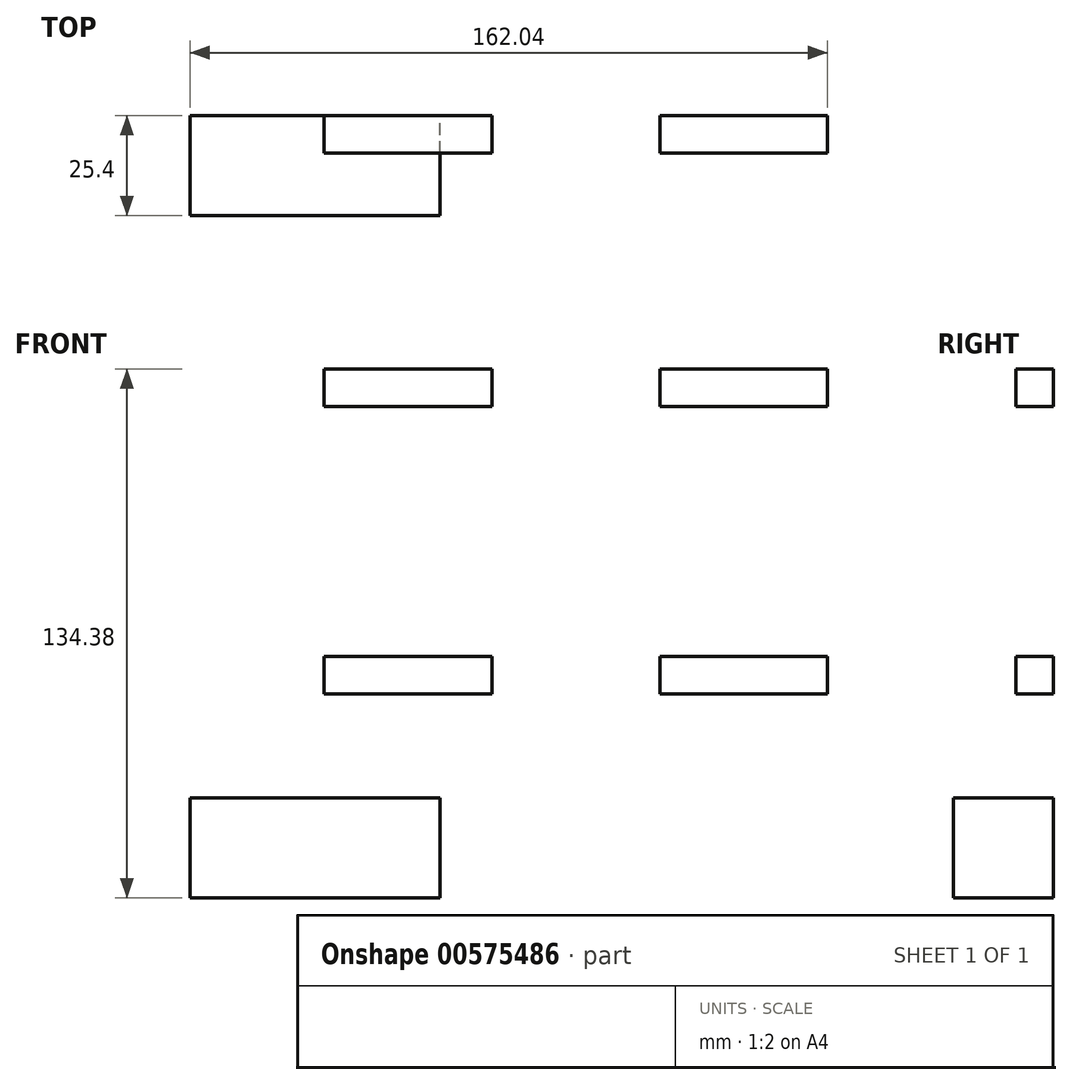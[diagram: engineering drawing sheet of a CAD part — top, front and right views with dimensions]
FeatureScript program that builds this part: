
annotation { "Feature Type Name" : "Feature", "Feature Type Description" : "" }
export const myFeature = defineFeature(function(context is Context, id is Id, definition is map)
    precondition{}
    {
        {
            var Q0;
            Q0=qCreatedBy(makeId("Front.planeOp"),FACE);
            var sketch = newSketch(context, id + "F0", { "sketchPlane" : qUnion([Q0])});
            skLineSegment(sketch, "E0.bottom", {"start": v(-119, 86.33) * mm, "end": v(51.66, 86.33) * mm});
            skLineSegment(sketch, "E0.top", {"start": v(-119, 3.78) * mm, "end": v(51.66, 3.78) * mm});
            skLineSegment(sketch, "E0.left", {"start": v(-119, 86.33) * mm, "end": v(-119, 3.78) * mm});
            skLineSegment(sketch, "E0.right", {"start": v(51.66, 86.33) * mm, "end": v(51.66, 3.78) * mm});
            skLineSegment(sketch, "E1.bottom", {"start": v(-119, 3.78) * mm, "end": v(-76.34, 3.78) * mm});
            skLineSegment(sketch, "E1.top", {"start": v(-119, 13.3) * mm, "end": v(-76.34, 13.3) * mm});
            skLineSegment(sketch, "E1.left", {"start": v(-119, 3.78) * mm, "end": v(-119, 13.3) * mm});
            skLineSegment(sketch, "E1.right", {"start": v(-76.34, 3.78) * mm, "end": v(-76.34, 13.3) * mm});
            skLineSegment(sketch, "E2.bottom", {"start": v(-76.34, 13.3) * mm, "end": v(-33.67, 13.3) * mm});
            skLineSegment(sketch, "E2.top", {"start": v(-76.34, 3.78) * mm, "end": v(-33.67, 3.78) * mm});
            skLineSegment(sketch, "E2.left", {"start": v(-76.34, 13.3) * mm, "end": v(-76.34, 3.78) * mm});
            skLineSegment(sketch, "E2.right", {"start": v(-33.67, 13.3) * mm, "end": v(-33.67, 3.78) * mm});
            skLineSegment(sketch, "E3.bottom", {"start": v(-33.67, 13.3) * mm, "end": v(9, 13.3) * mm});
            skLineSegment(sketch, "E3.top", {"start": v(-33.67, 3.78) * mm, "end": v(9, 3.78) * mm});
            skLineSegment(sketch, "E3.right", {"start": v(9, 13.3) * mm, "end": v(9, 3.78) * mm});
            skLineSegment(sketch, "E4.bottom", {"start": v(9, 13.3) * mm, "end": v(51.66, 13.3) * mm});
            skLineSegment(sketch, "E4.top", {"start": v(9, 3.78) * mm, "end": v(51.66, 3.78) * mm});
            skLineSegment(sketch, "E4.right", {"start": v(51.66, 13.3) * mm, "end": v(51.66, 3.78) * mm});
            skText(sketch, "E5", { "text": "1.67975\n", "fontName": "OpenSans-Regular.ttf"});
            skLineSegment(sketch, "E6.bottom", {"start": v(-119, 86.33) * mm, "end": v(-76.34, 86.33) * mm});
            skLineSegment(sketch, "E6.top", {"start": v(-119, 76.8) * mm, "end": v(-76.34, 76.8) * mm});
            skLineSegment(sketch, "E6.left", {"start": v(-119, 86.33) * mm, "end": v(-119, 76.8) * mm});
            skLineSegment(sketch, "E6.right", {"start": v(-76.34, 86.33) * mm, "end": v(-76.34, 76.8) * mm});
            skLineSegment(sketch, "E7.bottom", {"start": v(-76.34, 76.8) * mm, "end": v(-33.67, 76.8) * mm});
            skLineSegment(sketch, "E7.top", {"start": v(-76.34, 86.33) * mm, "end": v(-33.67, 86.33) * mm});
            skLineSegment(sketch, "E7.left", {"start": v(-76.34, 76.8) * mm, "end": v(-76.34, 86.33) * mm});
            skLineSegment(sketch, "E7.right", {"start": v(-33.67, 76.8) * mm, "end": v(-33.67, 86.33) * mm});
            skLineSegment(sketch, "E8.bottom", {"start": v(-33.67, 76.8) * mm, "end": v(9, 76.8) * mm});
            skLineSegment(sketch, "E8.top", {"start": v(-33.67, 86.33) * mm, "end": v(9, 86.33) * mm});
            skLineSegment(sketch, "E8.right", {"start": v(9, 76.8) * mm, "end": v(9, 86.33) * mm});
            skLineSegment(sketch, "E9.bottom", {"start": v(9, 76.8) * mm, "end": v(51.66, 76.8) * mm});
            skLineSegment(sketch, "E9.top", {"start": v(9, 86.33) * mm, "end": v(51.66, 86.33) * mm});
            skLineSegment(sketch, "E9.right", {"start": v(51.66, 76.8) * mm, "end": v(51.66, 86.33) * mm});
            const initialGuessF0  = {"E5": [0.06084, 0.0999, 1, 0, 0.01723]};
            skSetInitialGuess(sketch, initialGuessF0);
            skSolve(sketch);
        }
        {
            var Q0;
            Q0=makeQuery(id+"F0.imprint","IMPRINT",FACE,{"disambiguationData":[TD([[makeQuery(id+"F0.imprint","IMPRINT",EDGE,{"derivedFrom":sQuery(id+"F0.wireOp",EDGE,"E0.left")}),1.0]])]});
            extrude(context, id + "F1", {"entities" : qUnion([Q0]), "depth" : 9.52 * mm, "offsetDistance" : 25.4 * mm});
        }
        {
            var Q0;
            Q0=makeQuery(id+"F0.imprint","IMPRINT",FACE,{"disambiguationData":[TD([[makeQuery(id+"F0.imprint","IMPRINT",EDGE,{"derivedFrom":sQuery(id+"F0.wireOp",EDGE,"E1.bottom")}),1.0]])]});
            var Q1;
            Q1=makeQuery(id+"F0.imprint","IMPRINT",FACE,{"disambiguationData":[TD([[makeQuery(id+"F0.imprint","IMPRINT",EDGE,{"derivedFrom":sQuery(id+"F0.wireOp",EDGE,"E3.bottom")}),-1.0]])]});
            var Q2;
            Q2=makeQuery(id+"F0.imprint","IMPRINT",FACE,{"disambiguationData":[TD([[makeQuery(id+"F0.imprint","IMPRINT",EDGE,{"derivedFrom":sQuery(id+"F0.wireOp",EDGE,"E6.bottom")}),-1.0]])]});
            var Q3;
            Q3=makeQuery(id+"F0.imprint","IMPRINT",FACE,{"disambiguationData":[TD([[makeQuery(id+"F0.imprint","IMPRINT",EDGE,{"derivedFrom":sQuery(id+"F0.wireOp",EDGE,"E8.bottom")}),1.0]])]});
            extrude(context, id + "F2", {"entities" : qUnion([Q0, Q1, Q2, Q3]), "operationType" : NewBodyOperationType.ADD, "depth" : 9.52 * mm, "offsetDistance" : 25.4 * mm});
        }
        {
            var Q0;
            Q0=qCreatedBy(makeId("Front.planeOp"),FACE);
            var sketch = newSketch(context, id + "F3", { "sketchPlane" : qUnion([Q0])});
            skLineSegment(sketch, "E10.bottom", {"start": v(-153.05, -22.65) * mm, "end": v(-89.55, -22.65) * mm});
            skLineSegment(sketch, "E10.top", {"start": v(-153.05, -48.05) * mm, "end": v(-89.55, -48.05) * mm});
            skLineSegment(sketch, "E10.left", {"start": v(-153.05, -22.65) * mm, "end": v(-153.05, -48.05) * mm});
            skLineSegment(sketch, "E10.right", {"start": v(-89.55, -22.65) * mm, "end": v(-89.55, -48.05) * mm});
            skSolve(sketch);
        }
        {
            var Q0;
            Q0=makeQuery(id+"F3.imprint","IMPRINT",FACE,{"disambiguationData":[TD([[makeQuery(id+"F3.imprint","IMPRINT",EDGE,{"derivedFrom":sQuery(id+"F3.wireOp",EDGE,"E10.bottom")}),-1.0]])]});
            extrude(context, id + "F4", {"entities" : qUnion([Q0]), "depth" : 25.4 * mm, "offsetDistance" : 25.4 * mm});
        }
    });
